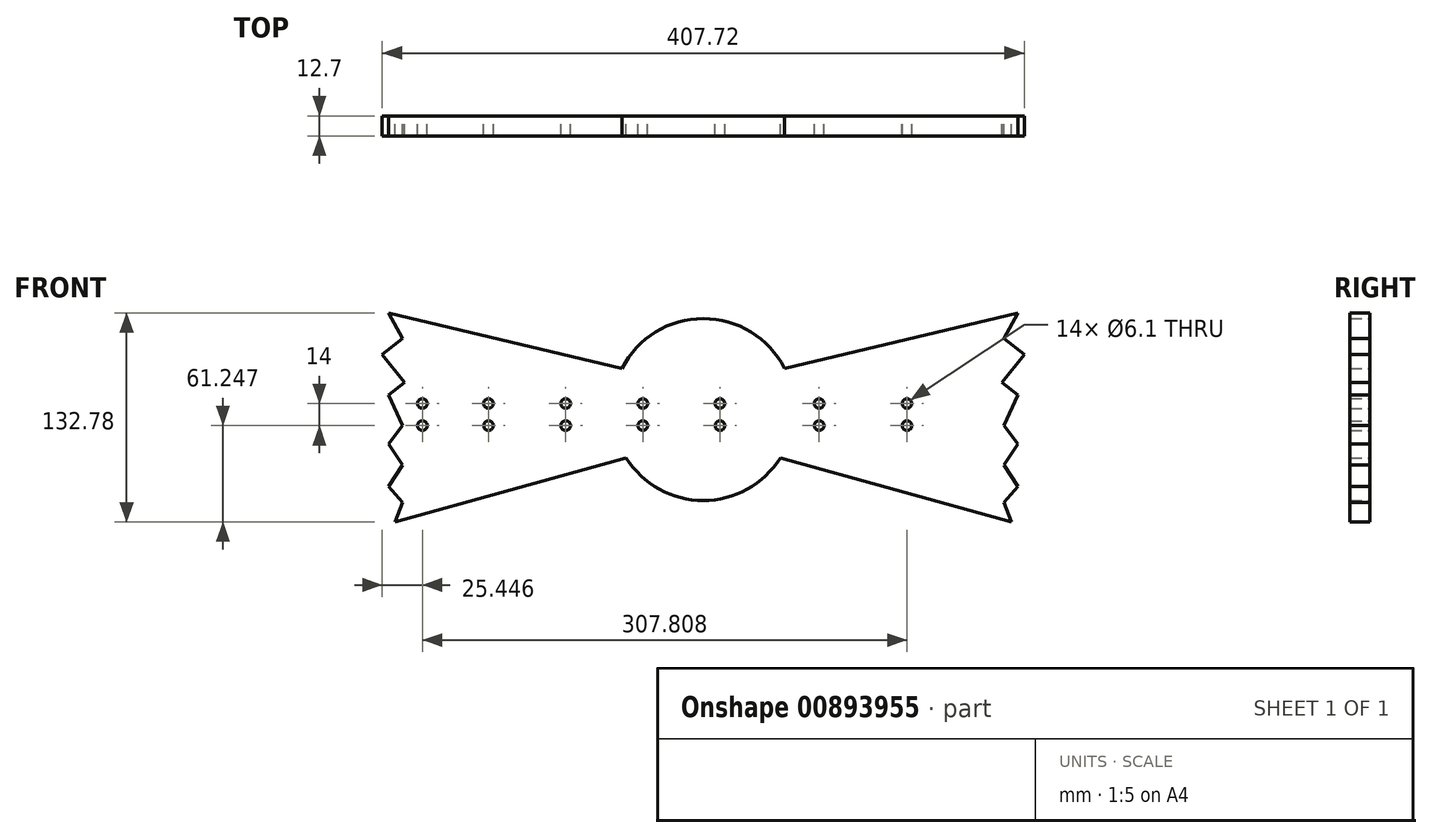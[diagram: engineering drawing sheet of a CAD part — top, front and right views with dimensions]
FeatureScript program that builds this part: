
annotation { "Feature Type Name" : "Feature", "Feature Type Description" : "" }
export const myFeature = defineFeature(function(context is Context, id is Id, definition is map)
    precondition{}
    {
        {
            var Q0;
            Q0=qCreatedBy(makeId("Front.planeOp"),FACE);
            var sketch = newSketch(context, id + "F0", { "sketchPlane" : qUnion([Q0])});
            skArc(sketch, "E0", {"start": v(0, 57.79) * mm, "mid": v(-30.2, 49.27) * mm, "end": v(-51.49, 26.23) * mm});
            skArc(sketch, "E1.trimOffspring", {"start": v(-48.94, -30.73) * mm, "mid": v(-27.96, -50.57) * mm, "end": v(0, -57.79) * mm});
            skArc(sketch, "E2.MirrorCS", {"start": v(0, 57.79) * mm, "mid": v(30.2, 49.27) * mm, "end": v(51.49, 26.23) * mm});
            skArc(sketch, "E3.MirrorCS", {"start": v(48.94, -30.73) * mm, "mid": v(27.96, -50.57) * mm, "end": v(0, -57.79) * mm});
            skLineSegment(sketch, "E4", {"start": v(51.49, 26.23) * mm, "end": v(199.78, 61.37) * mm});
            skLineSegment(sketch, "E5", {"start": v(48.94, -30.73) * mm, "end": v(195.8, -71.4) * mm});
            skLineSegment(sketch, "E6", {"start": v(199.78, 61.37) * mm, "end": v(191.02, 45) * mm});
            skLineSegment(sketch, "E7", {"start": v(191.02, 45) * mm, "end": v(203.86, 34.88) * mm});
            skLineSegment(sketch, "E8", {"start": v(203.86, 34.88) * mm, "end": v(189.84, 17.1) * mm});
            skLineSegment(sketch, "E9", {"start": v(189.84, 17.1) * mm, "end": v(199.78, 9.26) * mm});
            skLineSegment(sketch, "E10", {"start": v(199.78, 9.26) * mm, "end": v(191.02, -10.26) * mm});
            skLineSegment(sketch, "E11", {"start": v(191.02, -10.26) * mm, "end": v(199.78, -21.93) * mm});
            skLineSegment(sketch, "E12", {"start": v(199.78, -21.93) * mm, "end": v(191.02, -35.16) * mm});
            skLineSegment(sketch, "E13", {"start": v(191.02, -35.16) * mm, "end": v(199.78, -48.78) * mm});
            skLineSegment(sketch, "E14", {"start": v(199.78, -48.78) * mm, "end": v(191.02, -58.9) * mm});
            skLineSegment(sketch, "E15", {"start": v(191.02, -58.9) * mm, "end": v(195.8, -71.4) * mm});
            skLineSegment(sketch, "E16.MirrorCS", {"start": v(-48.94, -30.73) * mm, "end": v(-195.8, -71.4) * mm});
            skLineSegment(sketch, "E17.MirrorCS", {"start": v(-51.49, 26.23) * mm, "end": v(-199.78, 61.37) * mm});
            skLineSegment(sketch, "E18.MirrorCS", {"start": v(-191.02, 45) * mm, "end": v(-203.86, 34.88) * mm});
            skLineSegment(sketch, "E19.MirrorCS", {"start": v(-203.86, 34.88) * mm, "end": v(-189.84, 17.1) * mm});
            skLineSegment(sketch, "E20.MirrorCS", {"start": v(-189.84, 17.1) * mm, "end": v(-199.78, 9.26) * mm});
            skLineSegment(sketch, "E21.MirrorCS", {"start": v(-199.78, 9.26) * mm, "end": v(-191.02, -10.26) * mm});
            skLineSegment(sketch, "E22.MirrorCS", {"start": v(-191.02, -10.26) * mm, "end": v(-199.78, -21.93) * mm});
            skLineSegment(sketch, "E23.MirrorCS", {"start": v(-199.78, -21.93) * mm, "end": v(-191.02, -35.16) * mm});
            skLineSegment(sketch, "E24.MirrorCS", {"start": v(-191.02, -35.16) * mm, "end": v(-199.78, -48.78) * mm});
            skLineSegment(sketch, "E25.MirrorCS", {"start": v(-199.78, -48.78) * mm, "end": v(-191.02, -58.9) * mm});
            skLineSegment(sketch, "E26.MirrorCS", {"start": v(-191.02, -58.9) * mm, "end": v(-195.8, -71.4) * mm});
            skCircle(sketch, "E27.1.0.0", {"center": v(-178.4, -10.16) * mm, "radius": 3.05 * mm});
            skCircle(sketch, "E27.7.0.0", {"center": v(-136.4, -10.16) * mm, "radius": 3.05 * mm});
            skCircle(sketch, "E27.14.0.0", {"center": v(-87.4, -10.16) * mm, "radius": 3.05 * mm});
            skCircle(sketch, "E27.21.0.0", {"center": v(-38.4, -10.16) * mm, "radius": 3.05 * mm});
            skCircle(sketch, "E27.28.0.0", {"center": v(10.6, -10.16) * mm, "radius": 3.05 * mm});
            skCircle(sketch, "E27.37.0.0", {"center": v(73.6, -10.16) * mm, "radius": 3.05 * mm});
            skCircle(sketch, "E28.MirrorC", {"center": v(129.4, -10.16) * mm, "radius": 3.05 * mm});
            skCircle(sketch, "E29.MirrorC", {"center": v(-178.41, 3.84) * mm, "radius": 3.05 * mm});
            skCircle(sketch, "E30.MirrorC", {"center": v(-136.41, 3.84) * mm, "radius": 3.05 * mm});
            skCircle(sketch, "E31.MirrorC", {"center": v(-87.41, 3.84) * mm, "radius": 3.05 * mm});
            skCircle(sketch, "E32.MirrorC", {"center": v(-38.41, 3.84) * mm, "radius": 3.05 * mm});
            skCircle(sketch, "E33.MirrorC", {"center": v(10.59, 3.84) * mm, "radius": 3.05 * mm});
            skCircle(sketch, "E34.MirrorC", {"center": v(73.59, 3.84) * mm, "radius": 3.05 * mm});
            skCircle(sketch, "E35.MirrorC", {"center": v(129.38, 3.84) * mm, "radius": 3.05 * mm});
            skPoint(sketch, "E36.direction1.start.orphan", {"position": v(0, -100.95) * mm});
            skLineSegment(sketch, "E37.MirrorCS", {"start": v(-199.78, 61.37) * mm, "end": v(-191.02, 45) * mm});
            skPoint(sketch, "E38.MirrorC.center.orphan", {"position": v(143.88, 2.32) * mm});
            skPoint(sketch, "E39.MirrorC.center.orphan", {"position": v(143.88, 1.26) * mm});
            skSolve(sketch);
        }
        {
            var Q0;
            Q0=makeQuery(id+"F0.imprint","IMPRINT",FACE,{"disambiguationData":[TD([[makeQuery(id+"F0.imprint","IMPRINT",EDGE,{"derivedFrom":sQuery(id+"F0.wireOp",EDGE,"E0")}),1.0]])]});
            extrude(context, id + "F1", {"entities" : qUnion([Q0]), "depth" : 12.7 * mm, "offsetDistance" : 25.4 * mm});
        }
    });
